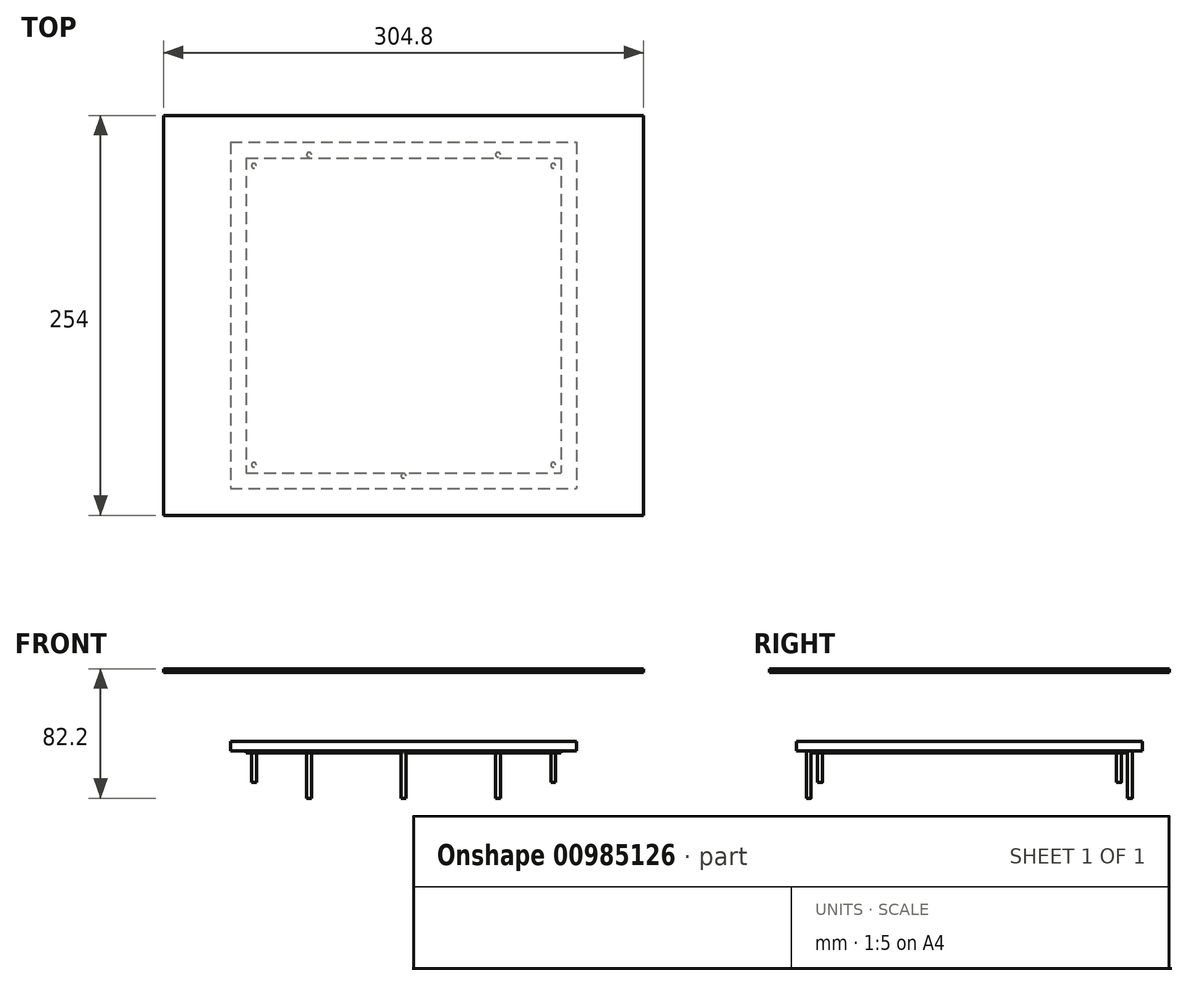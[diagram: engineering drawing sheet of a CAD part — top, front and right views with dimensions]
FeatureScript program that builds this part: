
annotation { "Feature Type Name" : "Feature", "Feature Type Description" : "" }
export const myFeature = defineFeature(function(context is Context, id is Id, definition is map)
    precondition{}
    {
        {
            var Q0;
            Q0=qCreatedBy(makeId("Top.planeOp"),FACE);
            var sketch = newSketch(context, id + "F0", { "sketchPlane" : qUnion([Q0])});
            skLineSegment(sketch, "E0.bottom", {"start": v(-110, 110) * mm, "end": v(110, 110) * mm});
            skLineSegment(sketch, "E0.top", {"start": v(-110, -110) * mm, "end": v(110, -110) * mm});
            skLineSegment(sketch, "E0.left", {"start": v(-110, 110) * mm, "end": v(-110, -110) * mm});
            skLineSegment(sketch, "E0.right", {"start": v(110, 110) * mm, "end": v(110, -110) * mm});
            skPoint(sketch, "E0.middle", {"position": v(0, 0) * mm});
            skLineSegment(sketch, "E1.bottom", {"start": v(-95, 95) * mm, "end": v(95, 95) * mm, "construction": true});
            skLineSegment(sketch, "E1.top", {"start": v(-95, -95) * mm, "end": v(95, -95) * mm, "construction": true});
            skLineSegment(sketch, "E1.left", {"start": v(-95, 95) * mm, "end": v(-95, -95) * mm, "construction": true});
            skLineSegment(sketch, "E1.right", {"start": v(95, 95) * mm, "end": v(95, -95) * mm, "construction": true});
            skLineSegment(sketch, "E2.bottom", {"start": v(-100, 100) * mm, "end": v(100, 100) * mm});
            skLineSegment(sketch, "E2.top", {"start": v(-100, -100) * mm, "end": v(100, -100) * mm});
            skLineSegment(sketch, "E2.left", {"start": v(-100, 100) * mm, "end": v(-100, -100) * mm});
            skLineSegment(sketch, "E2.right", {"start": v(100, 100) * mm, "end": v(100, -100) * mm});
            skLineSegment(sketch, "E3", {"start": v(-60, 110) * mm, "end": v(-60, -110) * mm, "construction": true});
            skLineSegment(sketch, "E4", {"start": v(60, 110) * mm, "end": v(60, -110) * mm, "construction": true});
            skLineSegment(sketch, "E5", {"start": v(0, 110) * mm, "end": v(0, -110) * mm, "construction": true});
            skLineSegment(sketch, "E6", {"start": v(-110, -102) * mm, "end": v(110, -102) * mm, "construction": true});
            skLineSegment(sketch, "E7", {"start": v(-110, 102) * mm, "end": v(110, 102) * mm, "construction": true});
            skCircle(sketch, "E8", {"center": v(-60, 102) * mm, "radius": 1.5 * mm});
            skCircle(sketch, "E9", {"center": v(60, 102) * mm, "radius": 1.5 * mm});
            skCircle(sketch, "E10", {"center": v(0, -102) * mm, "radius": 1.5 * mm});
            skCircle(sketch, "E11", {"center": v(-95, -95) * mm, "radius": 1.5 * mm});
            skCircle(sketch, "E12", {"center": v(95, -95) * mm, "radius": 1.5 * mm});
            skCircle(sketch, "E13", {"center": v(95, 95) * mm, "radius": 1.5 * mm});
            skCircle(sketch, "E14", {"center": v(-95, 95) * mm, "radius": 1.5 * mm});
            skLineSegment(sketch, "E15.bottom", {"start": v(-100, -100) * mm, "end": v(-60, -100) * mm, "construction": true});
            skLineSegment(sketch, "E15.top", {"start": v(-100, -60) * mm, "end": v(-60, -60) * mm, "construction": true});
            skLineSegment(sketch, "E15.left", {"start": v(-100, -100) * mm, "end": v(-100, -60) * mm, "construction": true});
            skLineSegment(sketch, "E15.right", {"start": v(-60, -100) * mm, "end": v(-60, -60) * mm, "construction": true});
            skLineSegment(sketch, "E16.bottom", {"start": v(100, -100) * mm, "end": v(60, -100) * mm, "construction": true});
            skLineSegment(sketch, "E16.top", {"start": v(100, -60) * mm, "end": v(60, -60) * mm, "construction": true});
            skLineSegment(sketch, "E16.left", {"start": v(100, -100) * mm, "end": v(100, -60) * mm, "construction": true});
            skLineSegment(sketch, "E16.right", {"start": v(60, -100) * mm, "end": v(60, -60) * mm, "construction": true});
            skLineSegment(sketch, "E17.bottom", {"start": v(-100, 100) * mm, "end": v(-60, 100) * mm, "construction": true});
            skLineSegment(sketch, "E17.top", {"start": v(-100, 60) * mm, "end": v(-60, 60) * mm, "construction": true});
            skLineSegment(sketch, "E17.left", {"start": v(-100, 100) * mm, "end": v(-100, 60) * mm, "construction": true});
            skLineSegment(sketch, "E17.right", {"start": v(-60, 100) * mm, "end": v(-60, 60) * mm, "construction": true});
            skLineSegment(sketch, "E18.bottom", {"start": v(100, 100) * mm, "end": v(60, 100) * mm, "construction": true});
            skLineSegment(sketch, "E18.top", {"start": v(100, 60) * mm, "end": v(60, 60) * mm, "construction": true});
            skLineSegment(sketch, "E18.left", {"start": v(100, 100) * mm, "end": v(100, 60) * mm, "construction": true});
            skLineSegment(sketch, "E18.right", {"start": v(60, 100) * mm, "end": v(60, 60) * mm, "construction": true});
            skLineSegment(sketch, "E19", {"start": v(-60, 60) * mm, "end": v(60, 60) * mm, "construction": true});
            skLineSegment(sketch, "E20", {"start": v(-60, -60) * mm, "end": v(60, -60) * mm, "construction": true});
            skSolve(sketch);
        }
        {
            var Q0;
            Q0=qSketchRegion(id+"F0",true);
            var Q1;
            Q1=makeQuery(id+"F0.imprint","IMPRINT",FACE,{"disambiguationData":[TD([[makeQuery(id+"F0.imprint","IMPRINT",EDGE,{"derivedFrom":sQuery(id+"F0.wireOp",EDGE,"E2.bottom")}),-1.0]])]});
            var Q2;
            Q2=makeQuery(id+"F0.imprint","IMPRINT",FACE,{"disambiguationData":[TD([[makeQuery(id+"F0.imprint","IMPRINT",EDGE,{"derivedFrom":sQuery(id+"F0.wireOp",EDGE,"E14")}),1.0]])]});
            var Q3;
            Q3=makeQuery(id+"F0.imprint","IMPRINT",FACE,{"disambiguationData":[TD([[makeQuery(id+"F0.imprint","IMPRINT",EDGE,{"derivedFrom":sQuery(id+"F0.wireOp",EDGE,"E8")}),1.0]])]});
            var Q4;
            Q4=makeQuery(id+"F0.imprint","IMPRINT",FACE,{"disambiguationData":[TD([[makeQuery(id+"F0.imprint","IMPRINT",EDGE,{"derivedFrom":sQuery(id+"F0.wireOp",EDGE,"E9")}),1.0]])]});
            var Q5;
            Q5=makeQuery(id+"F0.imprint","IMPRINT",FACE,{"disambiguationData":[TD([[makeQuery(id+"F0.imprint","IMPRINT",EDGE,{"derivedFrom":sQuery(id+"F0.wireOp",EDGE,"E13")}),1.0]])]});
            var Q6;
            Q6=makeQuery(id+"F0.imprint","IMPRINT",FACE,{"disambiguationData":[TD([[makeQuery(id+"F0.imprint","IMPRINT",EDGE,{"derivedFrom":sQuery(id+"F0.wireOp",EDGE,"E11")}),1.0]])]});
            var Q7;
            Q7=makeQuery(id+"F0.imprint","IMPRINT",FACE,{"disambiguationData":[TD([[makeQuery(id+"F0.imprint","IMPRINT",EDGE,{"derivedFrom":sQuery(id+"F0.wireOp",EDGE,"E10")}),1.0]])]});
            var Q8;
            Q8=makeQuery(id+"F0.imprint","IMPRINT",FACE,{"disambiguationData":[TD([[makeQuery(id+"F0.imprint","IMPRINT",EDGE,{"derivedFrom":sQuery(id+"F0.wireOp",EDGE,"E12")}),1.0]])]});
            extrude(context, id + "F1", {"entities" : qUnion([Q0, Q1, Q2, Q3, Q4, Q5, Q6, Q7, Q8]), "depth" : 6 * mm, "offsetDistance" : 25 * mm});
        }
        {
            var Q0;
            Q0=makeQuery(id+"F0.imprint","IMPRINT",FACE,{"disambiguationData":[TD([[makeQuery(id+"F0.imprint","IMPRINT",EDGE,{"derivedFrom":sQuery(id+"F0.wireOp",EDGE,"E2.bottom")}),-1.0]])]});
            extrude(context, id + "F2", {"entities" : qUnion([Q0]), "operationType" : NewBodyOperationType.ADD, "oppositeDirection" : true, "depth" : 1.4 * mm, "offsetDistance" : 25 * mm});
        }
        {
            var Q0;
            Q0=makeQuery(id+"F0.imprint","IMPRINT",FACE,{"disambiguationData":[TD([[makeQuery(id+"F0.imprint","IMPRINT",EDGE,{"derivedFrom":sQuery(id+"F0.wireOp",EDGE,"E11")}),1.0]])]});
            var Q1;
            Q1=makeQuery(id+"F0.imprint","IMPRINT",FACE,{"disambiguationData":[TD([[makeQuery(id+"F0.imprint","IMPRINT",EDGE,{"derivedFrom":sQuery(id+"F0.wireOp",EDGE,"E12")}),1.0]])]});
            var Q2;
            Q2=makeQuery(id+"F0.imprint","IMPRINT",FACE,{"disambiguationData":[TD([[makeQuery(id+"F0.imprint","IMPRINT",EDGE,{"derivedFrom":sQuery(id+"F0.wireOp",EDGE,"E14")}),1.0]])]});
            var Q3;
            Q3=makeQuery(id+"F0.imprint","IMPRINT",FACE,{"disambiguationData":[TD([[makeQuery(id+"F0.imprint","IMPRINT",EDGE,{"derivedFrom":sQuery(id+"F0.wireOp",EDGE,"E13")}),1.0]])]});
            extrude(context, id + "F3", {"entities" : qUnion([Q0, Q1, Q2, Q3]), "operationType" : NewBodyOperationType.ADD, "oppositeDirection" : true, "depth" : 20 * mm, "offsetDistance" : 25 * mm});
        }
        {
            var Q0;
            Q0=makeQuery(id+"F0.imprint","IMPRINT",FACE,{"disambiguationData":[TD([[makeQuery(id+"F0.imprint","IMPRINT",EDGE,{"derivedFrom":sQuery(id+"F0.wireOp",EDGE,"E10")}),1.0]])]});
            var Q1;
            Q1=makeQuery(id+"F0.imprint","IMPRINT",FACE,{"disambiguationData":[TD([[makeQuery(id+"F0.imprint","IMPRINT",EDGE,{"derivedFrom":sQuery(id+"F0.wireOp",EDGE,"E8")}),1.0]])]});
            var Q2;
            Q2=makeQuery(id+"F0.imprint","IMPRINT",FACE,{"disambiguationData":[TD([[makeQuery(id+"F0.imprint","IMPRINT",EDGE,{"derivedFrom":sQuery(id+"F0.wireOp",EDGE,"E9")}),1.0]])]});
            extrude(context, id + "F4", {"entities" : qUnion([Q0, Q1, Q2]), "operationType" : NewBodyOperationType.ADD, "oppositeDirection" : true, "depth" : 30 * mm, "offsetDistance" : 25 * mm});
        }
        {
            var Q0;
            Q0=makeQuery(id+"F1.opExtrude","CAP_FACE",FACE,{"disambiguationData":[OSD([sQuery(id+"F0.wireOp",EDGE,"E0.bottom"),sQuery(id+"F0.wireOp",EDGE,"E0.top"),sQuery(id+"F0.wireOp",EDGE,"E0.left"),sQuery(id+"F0.wireOp",EDGE,"E0.right")])],"isStart":false});
            var sketch = newSketch(context, id + "F5", { "sketchPlane" : qUnion([Q0])});
            skPoint(sketch, "E21.0", {"position": v(0, 0) * mm});
            skPoint(sketch, "E22.0", {"position": v(-60, -60) * mm});
            skPoint(sketch, "E22.1", {"position": v(-60, 60) * mm});
            skPoint(sketch, "E22.2", {"position": v(60, 60) * mm});
            skPoint(sketch, "E22.3", {"position": v(60, -60) * mm});
            skSolve(sketch);
        }
        {
            var Q0;
            Q0=qCreatedBy(makeId("Top.planeOp"),FACE);
            cPlane(context, id + "F6", {"entities" : qUnion([Q0]), "cplaneType" : CPlaneType.OFFSET, "offset" : 50 * mm, "width" : 150 * mm, "height" : 150 * mm});
        }
        {
            var Q0;
            Q0=qCreatedBy(id+"F6.planeOp",FACE);
            var sketch = newSketch(context, id + "F7", { "sketchPlane" : qUnion([Q0])});
            skLineSegment(sketch, "E23.bottom", {"start": v(-152.4, 127) * mm, "end": v(152.4, 127) * mm});
            skLineSegment(sketch, "E23.top", {"start": v(-152.4, -127) * mm, "end": v(152.4, -127) * mm});
            skLineSegment(sketch, "E23.left", {"start": v(-152.4, 127) * mm, "end": v(-152.4, -127) * mm});
            skLineSegment(sketch, "E23.right", {"start": v(152.4, 127) * mm, "end": v(152.4, -127) * mm});
            skPoint(sketch, "E23.middle", {"position": v(0, 0) * mm});
            skSolve(sketch);
        }
        {
            var Q0;
            Q0=makeQuery(id+"F7.imprint","IMPRINT",FACE,{"disambiguationData":[TD([[makeQuery(id+"F7.imprint","IMPRINT",EDGE,{"derivedFrom":sQuery(id+"F7.wireOp",EDGE,"E23.bottom")}),-1.0]])]});
            var Q1;
            Q1=makeQuery(id+"F7.imprint","IMPRINT",FACE,{"disambiguationData":[TD([[makeQuery(id+"F7.imprint","IMPRINT",EDGE,{"derivedFrom":makeQuery(id+"F1.opExtrude","CAP_EDGE",EDGE,{"disambiguationData":[OSD([sQuery(id+"F0.wireOp",EDGE,"E0.bottom")])],"isStart":false})}),-1.0]])]});
            extrude(context, id + "F8", {"entities" : qUnion([Q0, Q1]), "operationType" : NewBodyOperationType.ADD, "depth" : 2.2 * mm, "offsetDistance" : 25 * mm});
        }
    });
